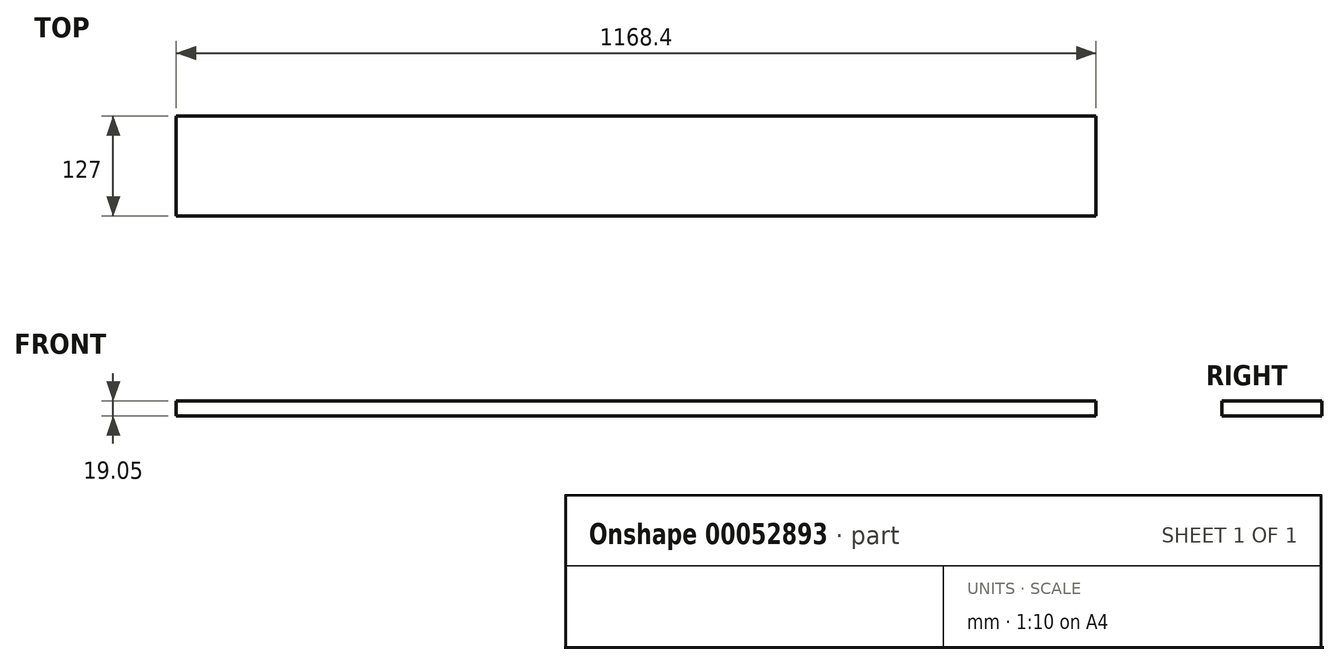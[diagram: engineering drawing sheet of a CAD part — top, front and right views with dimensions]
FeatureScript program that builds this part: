
annotation { "Feature Type Name" : "Feature", "Feature Type Description" : "" }
export const myFeature = defineFeature(function(context is Context, id is Id, definition is map)
    precondition{}
    {
        {
            var Q0;
            Q0=qCreatedBy(makeId("Top.planeOp"),FACE);
            var sketch = newSketch(context, id + "F0", { "sketchPlane" : qUnion([Q0])});
            skLineSegment(sketch, "E0.bottom", {"start": v(0, 0) * mm, "end": v(1168.4, 0) * mm});
            skLineSegment(sketch, "E0.top", {"start": v(0, 127) * mm, "end": v(1168.4, 127) * mm});
            skLineSegment(sketch, "E0.left", {"start": v(0, 0) * mm, "end": v(0, 127) * mm});
            skLineSegment(sketch, "E0.right", {"start": v(1168.4, 0) * mm, "end": v(1168.4, 127) * mm});
            skSolve(sketch);
        }
        {
            var Q0;
            Q0=makeQuery(id+"F0.imprint","IMPRINT",FACE,{"disambiguationData":[TD([[makeQuery(id+"F0.imprint","IMPRINT",EDGE,{"derivedFrom":sQuery(id+"F0.wireOp",EDGE,"E0.bottom")}),1.0]])]});
            extrude(context, id + "F1", {"entities" : qUnion([Q0]), "depth" : 19.05 * mm});
        }
    });
